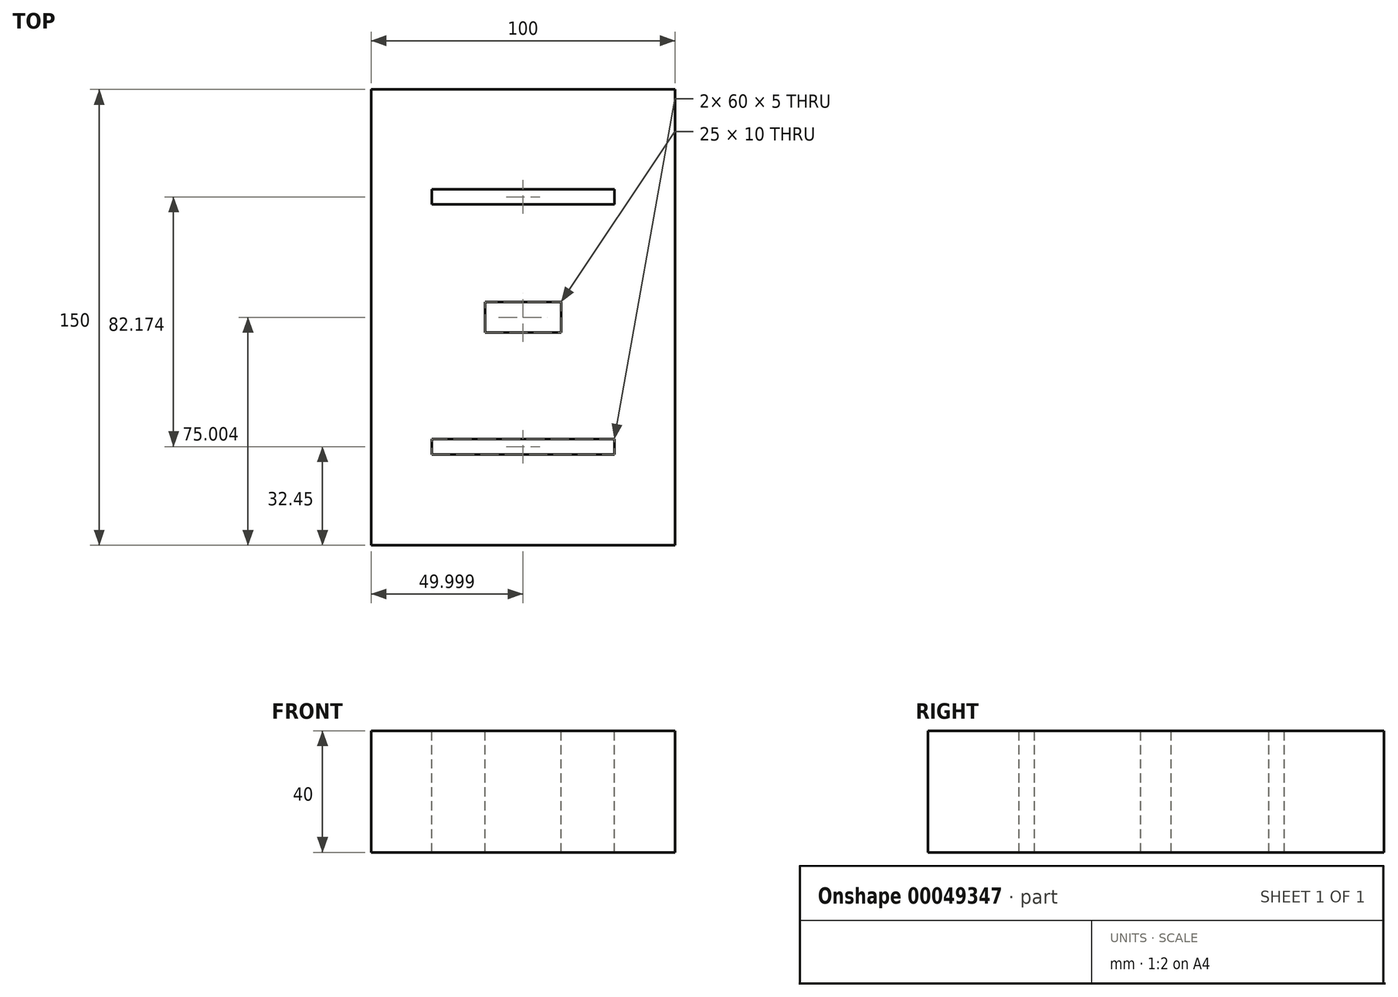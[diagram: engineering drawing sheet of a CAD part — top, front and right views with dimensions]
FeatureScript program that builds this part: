
annotation { "Feature Type Name" : "Feature", "Feature Type Description" : "" }
export const myFeature = defineFeature(function(context is Context, id is Id, definition is map)
    precondition{}
    {
        {
            var Q0;
            Q0=qCreatedBy(makeId("Top.planeOp"),FACE);
            var sketch = newSketch(context, id + "F0", { "sketchPlane" : qUnion([Q0])});
            skLineSegment(sketch, "E0.bottom", {"start": v(-105.84, 95.85) * mm, "end": v(-5.84, 95.85) * mm});
            skLineSegment(sketch, "E0.top", {"start": v(-105.84, -54.15) * mm, "end": v(-5.84, -54.15) * mm});
            skLineSegment(sketch, "E0.left", {"start": v(-105.84, 95.85) * mm, "end": v(-105.84, -54.15) * mm});
            skLineSegment(sketch, "E0.right", {"start": v(-5.84, 95.85) * mm, "end": v(-5.84, -54.15) * mm});
            skLineSegment(sketch, "E1.rect.bottom", {"start": v(-43.34, 15.85) * mm, "end": v(-68.34, 15.85) * mm});
            skLineSegment(sketch, "E1.rect.top", {"start": v(-43.34, 25.85) * mm, "end": v(-68.34, 25.85) * mm});
            skLineSegment(sketch, "E1.rect.left", {"start": v(-43.34, 15.85) * mm, "end": v(-43.34, 25.85) * mm});
            skLineSegment(sketch, "E1.rect.right", {"start": v(-68.34, 15.85) * mm, "end": v(-68.34, 25.85) * mm});
            skPoint(sketch, "E1.rect.middle", {"position": v(-55.84, 20.85) * mm});
            skPoint(sketch, "E1.rect.middle.positionSnap0", {"position": v(-55.84, 95.85) * mm});
            skPoint(sketch, "E1.rect.middle.positionSnap1", {"position": v(-105.84, 20.85) * mm});
            skPoint(sketch, "E1.rect.centerSnap0", {"position": v(-55.84, 95.85) * mm});
            skPoint(sketch, "E1.rect.centerSnap1", {"position": v(-105.84, 20.85) * mm});
            skLineSegment(sketch, "E2.rect.bottom", {"start": v(-25.84, 57.97) * mm, "end": v(-85.84, 57.97) * mm});
            skLineSegment(sketch, "E2.rect.top", {"start": v(-25.84, 62.97) * mm, "end": v(-85.84, 62.97) * mm});
            skLineSegment(sketch, "E2.rect.left", {"start": v(-25.84, 57.97) * mm, "end": v(-25.84, 62.97) * mm});
            skLineSegment(sketch, "E2.rect.right", {"start": v(-85.84, 57.97) * mm, "end": v(-85.84, 62.97) * mm});
            skPoint(sketch, "E2.rect.middle", {"position": v(-55.84, 60.47) * mm});
            skPoint(sketch, "E3.rect.middle", {"position": v(-55.84, -21.7) * mm});
            skLineSegment(sketch, "E3.rect.bottom", {"start": v(-25.84, -24.2) * mm, "end": v(-85.84, -24.2) * mm});
            skLineSegment(sketch, "E3.rect.top", {"start": v(-25.84, -19.2) * mm, "end": v(-85.84, -19.2) * mm});
            skLineSegment(sketch, "E3.rect.left", {"start": v(-25.84, -24.2) * mm, "end": v(-25.84, -19.2) * mm});
            skLineSegment(sketch, "E3.rect.right", {"start": v(-85.84, -24.2) * mm, "end": v(-85.84, -19.2) * mm});
            skPoint(sketch, "E4", {"position": v(-55.84, -54.15) * mm});
            skLineSegment(sketch, "E5.rect.bottom", {"start": v(-58.88, 25.85) * mm, "end": v(-52.8, 25.85) * mm});
            skLineSegment(sketch, "E5.rect.top", {"start": v(-58.88, 15.85) * mm, "end": v(-52.8, 15.85) * mm});
            skLineSegment(sketch, "E5.rect.left", {"start": v(-58.88, 25.85) * mm, "end": v(-58.88, 15.85) * mm});
            skLineSegment(sketch, "E5.rect.right", {"start": v(-52.8, 25.85) * mm, "end": v(-52.8, 15.85) * mm});
            skSolve(sketch);
        }
        {
            var Q0;
            Q0=makeQuery(id+"F0.imprint","IMPRINT",FACE,{"disambiguationData":[TD([[makeQuery(id+"F0.imprint","IMPRINT",EDGE,{"derivedFrom":sQuery(id+"F0.wireOp",EDGE,"E0.bottom")}),-1.0]])]});
            var Q1;
            Q1=makeQuery(id+"F0.imprint","IMPRINT",FACE,{"disambiguationData":[TD([[makeQuery(id+"F0.imprint","IMPRINT",EDGE,{"derivedFrom":sQuery(id+"F0.wireOp",EDGE,"E5.rect.bottom")}),-1.0]])]});
            extrude(context, id + "F1", {"entities" : qUnion([Q0, Q1]), "oppositeDirection" : true, "depth" : 40 * mm});
        }
    });
